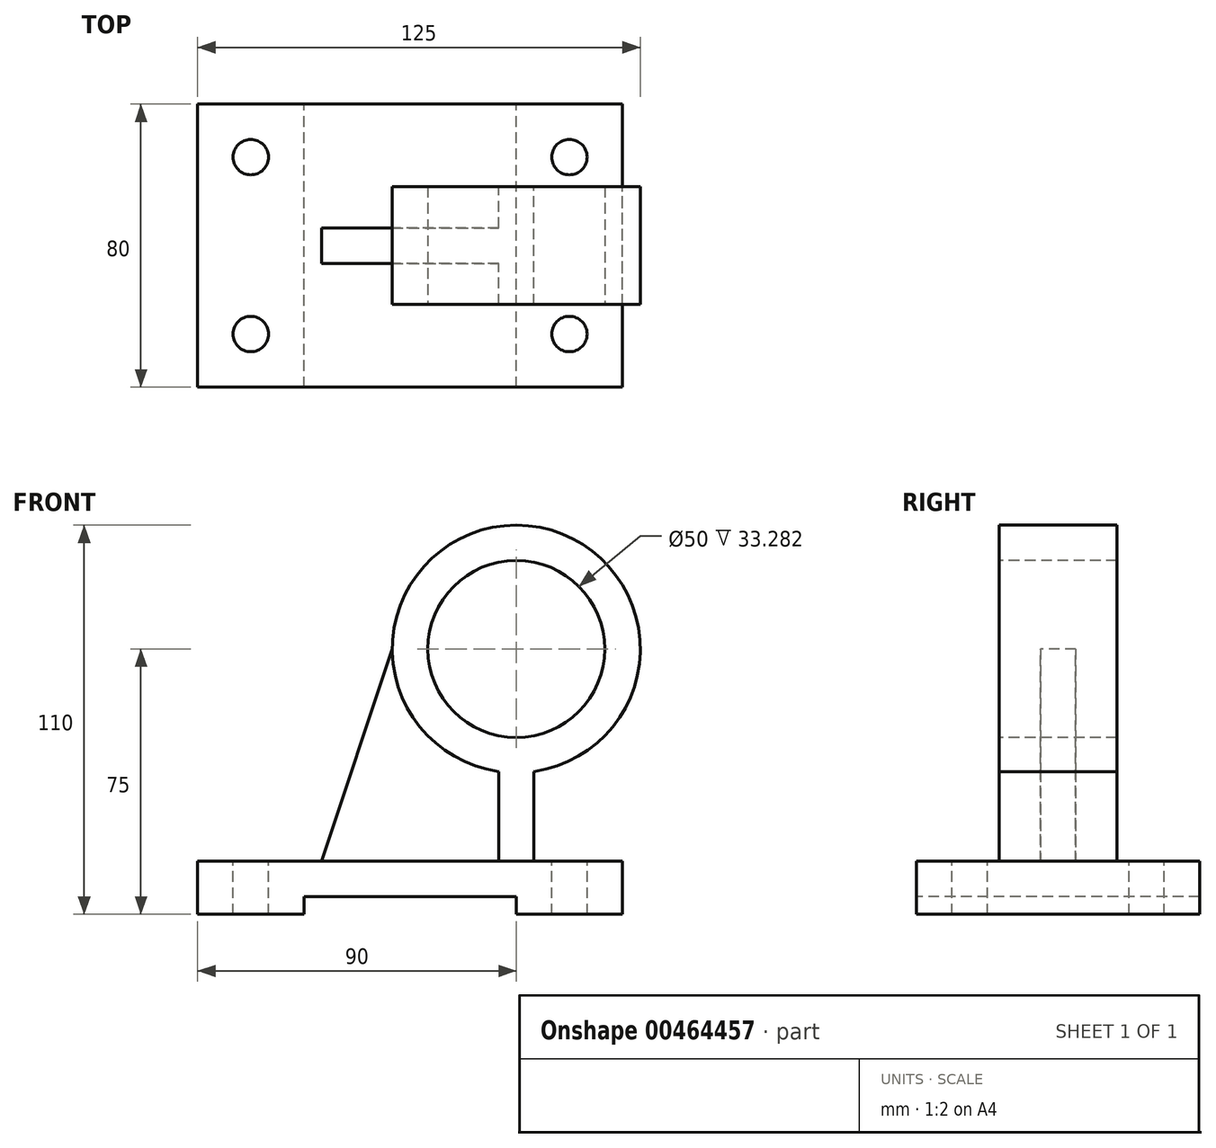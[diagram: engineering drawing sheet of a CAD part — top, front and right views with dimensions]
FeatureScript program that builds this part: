
annotation { "Feature Type Name" : "Feature", "Feature Type Description" : "" }
export const myFeature = defineFeature(function(context is Context, id is Id, definition is map)
    precondition{}
    {
        {
            var Q0;
            Q0=qCreatedBy(makeId("Top.planeOp"),FACE);
            var sketch = newSketch(context, id + "F0", { "sketchPlane" : qUnion([Q0])});
            skLineSegment(sketch, "E0.bottom", {"start": v(60, -40) * mm, "end": v(-60, -40) * mm});
            skLineSegment(sketch, "E0.top", {"start": v(60, 40) * mm, "end": v(-60, 40) * mm});
            skLineSegment(sketch, "E0.left", {"start": v(60, -40) * mm, "end": v(60, 40) * mm});
            skLineSegment(sketch, "E0.right", {"start": v(-60, -40) * mm, "end": v(-60, 40) * mm});
            skPoint(sketch, "E0.middle", {"position": v(0, 0) * mm});
            skSolve(sketch);
        }
        {
            var Q0;
            Q0=makeQuery(id+"F0.imprint","IMPRINT",FACE,{"disambiguationData":[TD([[makeQuery(id+"F0.imprint","IMPRINT",EDGE,{"derivedFrom":sQuery(id+"F0.wireOp",EDGE,"E0.bottom")}),-1.0]])]});
            extrude(context, id + "F1", {"entities" : qUnion([Q0]), "depth" : 15 * mm, "offsetDistance" : 25 * mm});
        }
        {
            var Q0;
            Q0=makeQuery(id+"F1.opExtrude","SWEPT_FACE",FACE,{"disambiguationData":[OSD([sQuery(id+"F0.wireOp",EDGE,"E0.bottom")])]});
            var sketch = newSketch(context, id + "F2", { "sketchPlane" : qUnion([Q0])});
            skLineSegment(sketch, "E1.bottom", {"start": v(30, -5) * mm, "end": v(-30, -5) * mm});
            skLineSegment(sketch, "E1.top", {"start": v(30, 5) * mm, "end": v(-30, 5) * mm});
            skLineSegment(sketch, "E1.left", {"start": v(30, -5) * mm, "end": v(30, 5) * mm});
            skLineSegment(sketch, "E1.right", {"start": v(-30, -5) * mm, "end": v(-30, 5) * mm});
            skPoint(sketch, "E1.middle", {"position": v(0, 0) * mm});
            skSolve(sketch);
        }
        {
            var Q0;
            Q0 = qSketchRegion(id + "F2", true);
            extrude(context, id + "F3", {"entities" : qUnion([Q0]), "operationType" : NewBodyOperationType.REMOVE, "endBound" : BoundingType.THROUGH_ALL, "oppositeDirection" : true, "depth" : 25 * mm, "offsetDistance" : 25 * mm});
        }
        {
            var Q0;
            Q0=makeQuery(id+"F1.opExtrude","CAP_FACE",FACE,{"disambiguationData":[OSD([sQuery(id+"F0.wireOp",EDGE,"E0.bottom"),sQuery(id+"F0.wireOp",EDGE,"E0.top"),sQuery(id+"F0.wireOp",EDGE,"E0.left"),sQuery(id+"F0.wireOp",EDGE,"E0.right")])],"isStart":false});
            var sketch = newSketch(context, id + "F4", { "sketchPlane" : qUnion([Q0])});
            skCircle(sketch, "E2", {"center": v(-45, 25) * mm, "radius": 5 * mm});
            skCircle(sketch, "E3.0.1.0", {"center": v(-45, -25) * mm, "radius": 5 * mm});
            skCircle(sketch, "E3.1.0.0", {"center": v(45, 25) * mm, "radius": 5 * mm});
            skCircle(sketch, "E3.1.1.0", {"center": v(45, -25) * mm, "radius": 5 * mm});
            skLineSegment(sketch, "E3.direction1", {"start": v(-45, 25) * mm, "end": v(45, 25) * mm, "construction": true});
            skLineSegment(sketch, "E3.direction2", {"start": v(-45, 25) * mm, "end": v(-45, -25) * mm, "construction": true});
            skSolve(sketch);
        }
        {
            var Q0;
            Q0=sQuery(id+"F4.wireOp",VERTEX,"E2.center");
            var Q1;
            Q1=sQuery(id+"F4.wireOp",VERTEX,"E3.direction1.end");
            var Q2;
            Q2=sQuery(id+"F4.wireOp",VERTEX,"E3.0.1.0.center");
            var Q3;
            Q3=sQuery(id+"F4.wireOp",VERTEX,"E3.1.1.0.center");
            var Q4;
            Q4=makeQuery(id+"F1.opExtrude","SWEPT_BODY",BODY,{"disambiguationData":[OSD([sQuery(id+"F0.wireOp",EDGE,"E0.bottom"),sQuery(id+"F0.wireOp",EDGE,"E0.top"),sQuery(id+"F0.wireOp",EDGE,"E0.left"),sQuery(id+"F0.wireOp",EDGE,"E0.right")])]});
            hole(context, id + "F5", {"style" : HoleStyle.SIMPLE, "endStyle" : HoleEndStyle.THROUGH, "holeDiameter" : 10 * mm, "majorDiameter" : 5 * mm, "isTappedThrough" : true, "tappedDepth" : 12 * mm, "tapClearance" : 3, "locations" : qUnion([Q0, Q1, Q2, Q3]), "scope" : qUnion([Q4])});
        }
        {
            var Q0;
            Q0=makeQuery(id+"F1.opExtrude","CAP_FACE",FACE,{"disambiguationData":[OSD([sQuery(id+"F0.wireOp",EDGE,"E0.bottom"),sQuery(id+"F0.wireOp",EDGE,"E0.top"),sQuery(id+"F0.wireOp",EDGE,"E0.left"),sQuery(id+"F0.wireOp",EDGE,"E0.right")])],"isStart":false});
            var sketch = newSketch(context, id + "F6", { "sketchPlane" : qUnion([Q0])});
            skLineSegment(sketch, "E4", {"start": v(-60, 0) * mm, "end": v(60, 0) * mm, "construction": true});
            skLineSegment(sketch, "E5.bottom", {"start": v(25, -5) * mm, "end": v(-25, -5) * mm});
            skLineSegment(sketch, "E5.top", {"start": v(25, 5) * mm, "end": v(-25, 5) * mm});
            skLineSegment(sketch, "E5.left", {"start": v(35, -5) * mm, "end": v(35, 5) * mm});
            skLineSegment(sketch, "E5.right", {"start": v(-25, -5) * mm, "end": v(-25, 5) * mm});
            skPoint(sketch, "E5.middle", {"position": v(5, 0) * mm});
            skLineSegment(sketch, "E6.bottom", {"start": v(35, -16.64) * mm, "end": v(25, -16.64) * mm});
            skLineSegment(sketch, "E6.top", {"start": v(35, 16.64) * mm, "end": v(25, 16.64) * mm});
            skLineSegment(sketch, "E6.left", {"start": v(35, -16.64) * mm, "end": v(35, 16.64) * mm});
            skLineSegment(sketch, "E6.right", {"start": v(25, -16.64) * mm, "end": v(25, -5) * mm});
            skPoint(sketch, "E6.middle", {"position": v(30, 0) * mm});
            skLineSegment(sketch, "E7.trimOffspring", {"start": v(25, 5) * mm, "end": v(25, 16.64) * mm});
            skSolve(sketch);
        }
        {
            var Q0;
            Q0 = qSketchRegion(id + "F6", true);
            extrude(context, id + "F7", {"entities" : qUnion([Q0]), "operationType" : NewBodyOperationType.ADD, "depth" : 60 * mm, "offsetDistance" : 25 * mm});
        }
        {
            var Q0;
            Q0=makeQuery(id+"F7.opExtrude","SWEPT_FACE",FACE,{"disambiguationData":[OSD([sQuery(id+"F6.wireOp",EDGE,"E6.bottom")])]});
            var sketch = newSketch(context, id + "F8", { "sketchPlane" : qUnion([Q0])});
            skCircle(sketch, "E8", {"center": v(30, 75) * mm, "radius": 35 * mm});
            skSolve(sketch);
        }
        {
            var Q0;
            Q0 = qSketchRegion(id + "F8", true);
            var Q1;
            Q1=makeQuery(id+"F7.opExtrude","SWEPT_FACE",FACE,{"disambiguationData":[OSD([sQuery(id+"F6.wireOp",EDGE,"E6.top")])]});
            extrude(context, id + "F9", {"entities" : qUnion([Q0]), "operationType" : NewBodyOperationType.ADD, "endBound" : BoundingType.UP_TO_SURFACE, "oppositeDirection" : true, "depth" : 25 * mm, "endBoundEntityFace" : qUnion([Q1]), "offsetDistance" : 25 * mm});
        }
        {
            var Q0;
            Q0=makeQuery(id+"F9.boolean.opBoolean","MERGE",FACE,{"derivedFrom":[makeQuery(id+"F7.opExtrude","SWEPT_FACE",FACE,{"disambiguationData":[OSD([sQuery(id+"F6.wireOp",EDGE,"E6.bottom")])]}),makeQuery(id+"F9.opExtrude","CAP_FACE",FACE,{"disambiguationData":[OSD([sQuery(id+"F8.wireOp",EDGE,"E8")])],"isStart":true})]});
            var sketch = newSketch(context, id + "F10", { "sketchPlane" : qUnion([Q0])});
            skCircle(sketch, "E9", {"center": v(30, 75) * mm, "radius": 25 * mm});
            skSolve(sketch);
        }
        {
            var Q0;
            Q0 = qSketchRegion(id + "F10", true);
            extrude(context, id + "F11", {"entities" : qUnion([Q0]), "operationType" : NewBodyOperationType.REMOVE, "endBound" : BoundingType.THROUGH_ALL, "oppositeDirection" : true, "depth" : 25 * mm, "offsetDistance" : 25 * mm});
        }
        {
            var Q0;
            Q0=makeQuery(id+"F7.opExtrude","SWEPT_FACE",FACE,{"disambiguationData":[OSD([sQuery(id+"F6.wireOp",EDGE,"E5.bottom")])]});
            var sketch = newSketch(context, id + "F12", { "sketchPlane" : qUnion([Q0])});
            skLineSegment(sketch, "E10", {"start": v(-25, 15) * mm, "end": v(-5, 75) * mm});
            skLineSegment(sketch, "E11", {"start": v(-5, 75) * mm, "end": v(-25, 75) * mm});
            skLineSegment(sketch, "E12", {"start": v(-25, 75) * mm, "end": v(-25, 16.94) * mm});
            skSolve(sketch);
        }
        {
            var Q0;
            {var subQ0=sQuery(id+"F12.wireOp",EDGE,"E10");Q0=makeQuery(id+"F12.imprint","IMPRINT",FACE,{"disambiguationData":[TD([[makeQuery(id+"F12.imprint","IMPRINT",EDGE,{"derivedFrom":subQ0}),1.0]])]});}
            extrude(context, id + "F13", {"entities" : qUnion([Q0]), "operationType" : NewBodyOperationType.REMOVE, "oppositeDirection" : true, "depth" : 25 * mm, "offsetDistance" : 25 * mm});
        }
    });
